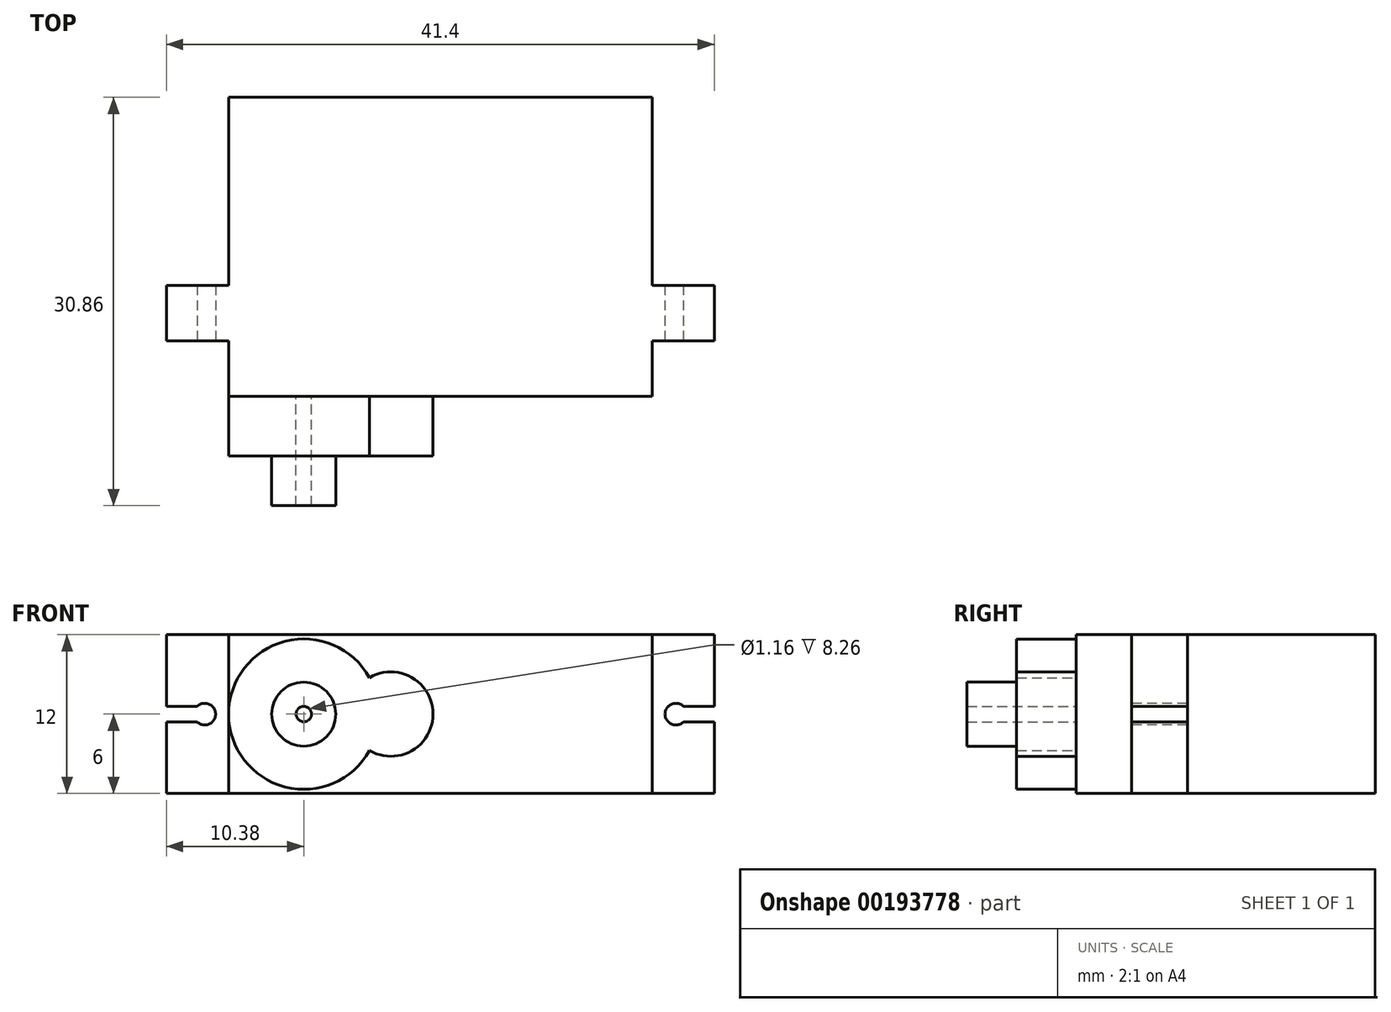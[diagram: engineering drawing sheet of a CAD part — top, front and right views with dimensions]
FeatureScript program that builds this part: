
annotation { "Feature Type Name" : "Feature", "Feature Type Description" : "" }
export const myFeature = defineFeature(function(context is Context, id is Id, definition is map)
    precondition{}
    {
        {
            var Q0;
            Q0=qCreatedBy(makeId("Top.planeOp"),FACE);
            var sketch = newSketch(context, id + "F0", { "sketchPlane" : qUnion([Q0])});
            skLineSegment(sketch, "E0.bottom", {"start": v(16, -11.3) * mm, "end": v(-16, -11.3) * mm});
            skLineSegment(sketch, "E0.top", {"start": v(16, 11.3) * mm, "end": v(-16, 11.3) * mm});
            skLineSegment(sketch, "E0.left", {"start": v(16, -11.3) * mm, "end": v(16, 11.3) * mm});
            skLineSegment(sketch, "E0.right", {"start": v(-16, -11.3) * mm, "end": v(-16, 11.3) * mm});
            skPoint(sketch, "E0.middle", {"position": v(0, 0) * mm});
            skSolve(sketch);
        }
        {
            var Q0;
            Q0=makeQuery(id+"F0.imprint","IMPRINT",FACE,{"disambiguationData":[TD([[makeQuery(id+"F0.imprint","IMPRINT",EDGE,{"derivedFrom":sQuery(id+"F0.wireOp",EDGE,"E0.bottom")}),-1.0]])]});
            extrude(context, id + "F1", {"entities" : qUnion([Q0]), "depth" : 12 * mm});
        }
        {
            var Q0;
            Q0=makeQuery(id+"F1.opExtrude","SWEPT_FACE",FACE,{"disambiguationData":[OSD([sQuery(id+"F0.wireOp",EDGE,"E0.bottom")])]});
            var sketch = newSketch(context, id + "F2", { "sketchPlane" : qUnion([Q0])});
            skLineSegment(sketch, "E1.bottom", {"start": v(-20.7, 12) * mm, "end": v(20.7, 12) * mm});
            skLineSegment(sketch, "E1.top", {"start": v(-20.7, 0) * mm, "end": v(20.7, 0) * mm});
            skLineSegment(sketch, "E1.left", {"start": v(-20.7, 12) * mm, "end": v(-20.7, 0) * mm});
            skLineSegment(sketch, "E1.right", {"start": v(20.7, 12) * mm, "end": v(20.7, 0) * mm});
            skLineSegment(sketch, "E2", {"start": v(-17.8, 12) * mm, "end": v(-17.8, 6.6) * mm, "construction": true});
            skLineSegment(sketch, "E3", {"start": v(-19.27, 0) * mm, "end": v(-19.27, 5.4) * mm, "construction": true});
            skCircle(sketch, "E4", {"center": v(-17.8, 6) * mm, "radius": 0.82 * mm});
            skLineSegment(sketch, "E5.bottom", {"start": v(-18.36, 6.6) * mm, "end": v(-20.7, 6.6) * mm});
            skLineSegment(sketch, "E5.top", {"start": v(-18.36, 5.4) * mm, "end": v(-20.7, 5.4) * mm});
            skLineSegment(sketch, "E5.right", {"start": v(-20.7, 6.6) * mm, "end": v(-20.7, 5.4) * mm});
            skLineSegment(sketch, "E6", {"start": v(0, 12) * mm, "end": v(0, -2.95) * mm, "construction": true});
            skPoint(sketch, "E6.endSnap0", {"position": v(0, 12) * mm});
            skCircle(sketch, "E7.MirrorC", {"center": v(17.8, 6) * mm, "radius": 0.82 * mm});
            skLineSegment(sketch, "E8.MirrorCS", {"start": v(18.36, 6.6) * mm, "end": v(20.7, 6.6) * mm});
            skLineSegment(sketch, "E9.MirrorCS", {"start": v(18.36, 5.4) * mm, "end": v(20.7, 5.4) * mm});
            skSolve(sketch);
        }
        {
            var Q0;
            {var subQ1=sQuery(id+"F0.wireOp",EDGE,"E0.bottom");var subQ2=makeQuery(id+"F1.opExtrude","SWEPT_EDGE",EDGE,{"disambiguationData":[OSD([subQ1,sQuery(id+"F0.wireOp",EDGE,"E0.left")])]});Q0=makeQuery(id+"F2.imprint","IMPRINT",FACE,{"disambiguationData":[TD([[makeQuery(id+"F2.imprint","IMPRINT",EDGE,{"derivedFrom":subQ2}),-1.0]])]});}
            var Q1;
            {var subQ7=sQuery(id+"F2.wireOp",EDGE,"E5.bottom");Q1=makeQuery(id+"F2.imprint","IMPRINT",FACE,{"disambiguationData":[TD([[makeQuery(id+"F2.imprint","IMPRINT",EDGE,{"derivedFrom":subQ7}),-1.0]])]});}
            var Q2;
            {var subQ7=sQuery(id+"F2.wireOp",EDGE,"E8.MirrorCS");Q2=makeQuery(id+"F2.imprint","IMPRINT",FACE,{"disambiguationData":[TD([[makeQuery(id+"F2.imprint","IMPRINT",EDGE,{"derivedFrom":subQ7}),1.0]])]});}
            extrude(context, id + "F3", {"entities" : qUnion([Q0, Q1, Q2]), "operationType" : NewBodyOperationType.ADD, "oppositeDirection" : true, "depth" : 8.4 * mm, "hasSecondDirection" : true, "secondDirectionOppositeDirection" : true, "secondDirectionDepth" : 4.2 * mm});
        }
        {
            var Q0;
            Q0=makeQuery(id+"F1.opExtrude","SWEPT_FACE",FACE,{"disambiguationData":[OSD([sQuery(id+"F0.wireOp",EDGE,"E0.bottom")])]});
            var sketch = newSketch(context, id + "F4", { "sketchPlane" : qUnion([Q0])});
            skLineSegment(sketch, "E10", {"start": v(-16, 6) * mm, "end": v(-10.32, 6) * mm, "construction": true});
            skCircle(sketch, "E11", {"center": v(-10.32, 6) * mm, "radius": 5.68 * mm});
            skLineSegment(sketch, "E12", {"start": v(-10.32, 6) * mm, "end": v(-3.74, 6) * mm, "construction": true});
            skCircle(sketch, "E13", {"center": v(-3.74, 6) * mm, "radius": 3.19 * mm});
            skCircle(sketch, "E14", {"center": v(-10.32, 6) * mm, "radius": 2.42 * mm});
            skCircle(sketch, "E15", {"center": v(-10.32, 6) * mm, "radius": 0.58 * mm});
            skSolve(sketch);
        }
        {
            var Q0;
            Q0 = qSketchRegion(id + "F4", true);
            var Q1;
            Q1=makeQuery(id+"F4.imprint","IMPRINT",FACE,{"disambiguationData":[TD([[makeQuery(id+"F4.imprint","IMPRINT",EDGE,{"derivedFrom":sQuery(id+"F4.wireOp",EDGE,"E14")}),1.0]])]});
            extrude(context, id + "F5", {"entities" : qUnion([Q0, Q1]), "operationType" : NewBodyOperationType.ADD, "depth" : 4.5 * mm});
        }
        {
            var Q0;
            Q0=makeQuery(id+"F5.opExtrude","CAP_FACE",FACE,{"disambiguationData":[OSD([sQuery(id+"F4.wireOp",EDGE,"E11"),sQuery(id+"F4.wireOp",EDGE,"E13")])],"isStart":false});
            var sketch = newSketch(context, id + "F6", { "sketchPlane" : qUnion([Q0])});
            skCircle(sketch, "E16", {"center": v(-10.32, 6) * mm, "radius": 2.42 * mm});
            skCircle(sketch, "E17", {"center": v(-10.32, 6) * mm, "radius": 0.58 * mm});
            skSolve(sketch);
        }
        {
            var Q0;
            Q0 = qSketchRegion(id + "F6", true);
            extrude(context, id + "F7", {"entities" : qUnion([Q0]), "operationType" : NewBodyOperationType.ADD, "depth" : 3.76 * mm});
        }
    });
